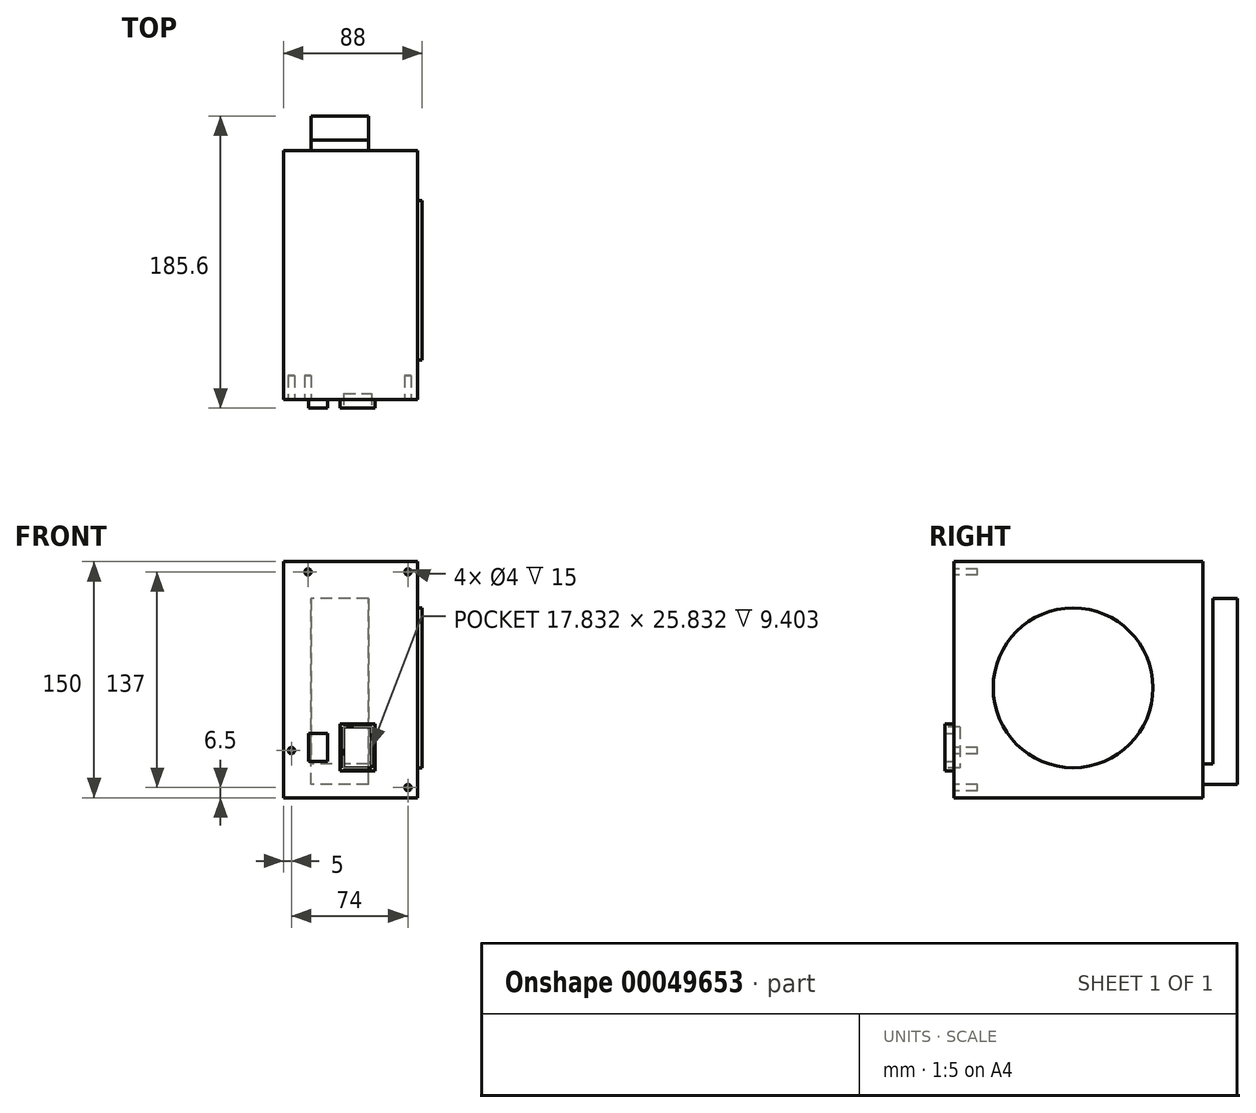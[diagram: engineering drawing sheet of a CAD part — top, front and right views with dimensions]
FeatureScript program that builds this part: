
annotation { "Feature Type Name" : "Feature", "Feature Type Description" : "" }
export const myFeature = defineFeature(function(context is Context, id is Id, definition is map)
    precondition{}
    {
        {
            var Q0;
            Q0=qCreatedBy(makeId("Front.planeOp"),FACE);
            var sketch = newSketch(context, id + "F0", { "sketchPlane" : qUnion([Q0])});
            skLineSegment(sketch, "E0.bottom", {"start": v(0, 0) * mm, "end": v(85, 0) * mm});
            skLineSegment(sketch, "E0.top", {"start": v(0, 150) * mm, "end": v(85, 150) * mm});
            skLineSegment(sketch, "E0.left", {"start": v(0, 0) * mm, "end": v(0, 150) * mm});
            skLineSegment(sketch, "E0.right", {"start": v(85, 0) * mm, "end": v(85, 150) * mm});
            skCircle(sketch, "E1", {"center": v(5, 30) * mm, "radius": 2 * mm});
            skCircle(sketch, "E2", {"center": v(15.5, 143.5) * mm, "radius": 2 * mm});
            skCircle(sketch, "E3", {"center": v(79, 143.5) * mm, "radius": 2 * mm});
            skCircle(sketch, "E4", {"center": v(79, 6.5) * mm, "radius": 2 * mm});
            skSolve(sketch);
        }
        {
            var Q0;
            Q0=makeQuery(id+"F0.imprint","IMPRINT",FACE,{"disambiguationData":[TD([[makeQuery(id+"F0.imprint","IMPRINT",EDGE,{"derivedFrom":sQuery(id+"F0.wireOp",EDGE,"E0.bottom")}),1.0]])]});
            var Q1;
            Q1=makeQuery(id+"F0.imprint","IMPRINT",FACE,{"disambiguationData":[TD([[makeQuery(id+"F0.imprint","IMPRINT",EDGE,{"derivedFrom":sQuery(id+"F0.wireOp",EDGE,"E2")}),1.0]])]});
            var Q2;
            Q2=makeQuery(id+"F0.imprint","IMPRINT",FACE,{"disambiguationData":[TD([[makeQuery(id+"F0.imprint","IMPRINT",EDGE,{"derivedFrom":sQuery(id+"F0.wireOp",EDGE,"E3")}),1.0]])]});
            var Q3;
            Q3=makeQuery(id+"F0.imprint","IMPRINT",FACE,{"disambiguationData":[TD([[makeQuery(id+"F0.imprint","IMPRINT",EDGE,{"derivedFrom":sQuery(id+"F0.wireOp",EDGE,"E4")}),1.0]])]});
            var Q4;
            Q4=makeQuery(id+"F0.imprint","IMPRINT",FACE,{"disambiguationData":[TD([[makeQuery(id+"F0.imprint","IMPRINT",EDGE,{"derivedFrom":sQuery(id+"F0.wireOp",EDGE,"E1")}),1.0]])]});
            extrude(context, id + "F1", {"entities" : qUnion([Q0, Q1, Q2, Q3, Q4]), "depth" : 158 * mm});
        }
        {
            var Q0;
            Q0=makeQuery(id+"F1.opExtrude","CAP_FACE",FACE,{"disambiguationData":[OSD([sQuery(id+"F0.wireOp",EDGE,"E0.bottom"),sQuery(id+"F0.wireOp",EDGE,"E0.top"),sQuery(id+"F0.wireOp",EDGE,"E0.left"),sQuery(id+"F0.wireOp",EDGE,"E0.right")])],"isStart":false});
            var sketch = newSketch(context, id + "F2", { "sketchPlane" : qUnion([Q0])});
            skCircle(sketch, "E5.0", {"center": v(79, 6.5) * mm, "radius": 2 * mm});
            skCircle(sketch, "E6.0", {"center": v(5, 30) * mm, "radius": 2 * mm});
            skCircle(sketch, "E7.0", {"center": v(15.5, 143.5) * mm, "radius": 2 * mm});
            skCircle(sketch, "E8.0", {"center": v(79, 143.5) * mm, "radius": 2 * mm});
            skSolve(sketch);
        }
        {
            var Q0;
            Q0 = qSketchRegion(id + "F2", true);
            extrude(context, id + "F3", {"entities" : qUnion([Q0]), "operationType" : NewBodyOperationType.REMOVE, "oppositeDirection" : true, "depth" : 15 * mm});
        }
        {
            var Q0;
            Q0=makeQuery(id+"F1.opExtrude","CAP_FACE",FACE,{"disambiguationData":[OSD([sQuery(id+"F0.wireOp",EDGE,"E0.bottom"),sQuery(id+"F0.wireOp",EDGE,"E0.top"),sQuery(id+"F0.wireOp",EDGE,"E0.left"),sQuery(id+"F0.wireOp",EDGE,"E0.right")])],"isStart":false});
            var sketch = newSketch(context, id + "F4", { "sketchPlane" : qUnion([Q0])});
            skLineSegment(sketch, "E9.bottom", {"start": v(58, 17) * mm, "end": v(36, 17) * mm});
            skLineSegment(sketch, "E9.top", {"start": v(58, 47) * mm, "end": v(36, 47) * mm});
            skLineSegment(sketch, "E9.left", {"start": v(58, 17) * mm, "end": v(58, 47) * mm});
            skLineSegment(sketch, "E9.right", {"start": v(36, 17) * mm, "end": v(36, 47) * mm});
            skLineSegment(sketch, "E10.bottom", {"start": v(28, 23) * mm, "end": v(16, 23) * mm});
            skLineSegment(sketch, "E10.top", {"start": v(28, 41) * mm, "end": v(16, 41) * mm});
            skLineSegment(sketch, "E10.left", {"start": v(28, 23) * mm, "end": v(28, 41) * mm});
            skLineSegment(sketch, "E10.right", {"start": v(16, 23) * mm, "end": v(16, 41) * mm});
            skSolve(sketch);
        }
        {
            var Q0;
            Q0=makeQuery(id+"F4.imprint","IMPRINT",FACE,{"disambiguationData":[TD([[makeQuery(id+"F4.imprint","IMPRINT",EDGE,{"derivedFrom":sQuery(id+"F4.wireOp",EDGE,"E10.bottom")}),-1.0]])]});
            var Q1;
            Q1=makeQuery(id+"F4.imprint","IMPRINT",FACE,{"disambiguationData":[TD([[makeQuery(id+"F4.imprint","IMPRINT",EDGE,{"derivedFrom":sQuery(id+"F4.wireOp",EDGE,"E9.bottom")}),-1.0]])]});
            extrude(context, id + "F5", {"entities" : qUnion([Q0, Q1]), "operationType" : NewBodyOperationType.ADD, "depth" : 5.6 * mm});
        }
        {
            var Q0;
            Q0=makeQuery(id+"F5.opExtrude","CAP_FACE",FACE,{"disambiguationData":[OSD([sQuery(id+"F4.wireOp",EDGE,"E9.bottom"),sQuery(id+"F4.wireOp",EDGE,"E9.top"),sQuery(id+"F4.wireOp",EDGE,"E9.left"),sQuery(id+"F4.wireOp",EDGE,"E9.right")])],"isStart":false});
            var sketch = newSketch(context, id + "F6", { "sketchPlane" : qUnion([Q0])});
            skLineSegment(sketch, "E11.0", {"start": v(38.08, 19.08) * mm, "end": v(55.92, 19.08) * mm});
            skLineSegment(sketch, "E11.1", {"start": v(38.08, 44.92) * mm, "end": v(38.08, 19.08) * mm});
            skLineSegment(sketch, "E11.2", {"start": v(55.92, 44.92) * mm, "end": v(38.08, 44.92) * mm});
            skLineSegment(sketch, "E11.3", {"start": v(55.92, 19.08) * mm, "end": v(55.92, 44.92) * mm});
            skSolve(sketch);
        }
        {
            var Q0;
            Q0=makeQuery(id+"F6.imprint","IMPRINT",FACE,{"disambiguationData":[TD([[makeQuery(id+"F6.imprint","IMPRINT",EDGE,{"derivedFrom":sQuery(id+"F6.wireOp",EDGE,"E11.0")}),1.0]])]});
            extrude(context, id + "F7", {"entities" : qUnion([Q0]), "operationType" : NewBodyOperationType.REMOVE, "oppositeDirection" : true, "depth" : 9.4 * mm});
        }
        {
            var Q0;
            Q0=makeQuery(id+"F1.opExtrude","SWEPT_FACE",FACE,{"disambiguationData":[OSD([sQuery(id+"F0.wireOp",EDGE,"E0.right")])]});
            var sketch = newSketch(context, id + "F8", { "sketchPlane" : qUnion([Q0])});
            skCircle(sketch, "E12", {"center": v(-82.33, 69.87) * mm, "radius": 50.72 * mm});
            skSolve(sketch);
        }
        {
            var Q0;
            Q0 = qSketchRegion(id + "F8", true);
            var Q1;
            Q1=makeQuery(id+"F8.imprint","IMPRINT",FACE,{"disambiguationData":[TD([[makeQuery(id+"F8.imprint","IMPRINT",EDGE,{"derivedFrom":sQuery(id+"F8.wireOp",EDGE,"E12")}),1.0]])]});
            extrude(context, id + "F9", {"entities" : qUnion([Q0, Q1]), "operationType" : NewBodyOperationType.ADD, "depth" : 3 * mm});
        }
        {
            var Q0;
            Q0=makeQuery(id+"F0.imprint","IMPRINT",FACE,{"disambiguationData":[TD([[makeQuery(id+"F0.imprint","IMPRINT",EDGE,{"derivedFrom":sQuery(id+"F0.wireOp",EDGE,"E0.bottom")}),1.0]])]});
            var sketch = newSketch(context, id + "F10", { "sketchPlane" : qUnion([Q0])});
            skLineSegment(sketch, "E13.bottom", {"start": v(53.93, 8.49) * mm, "end": v(17.55, 8.49) * mm});
            skLineSegment(sketch, "E13.top", {"start": v(53.93, 21.4) * mm, "end": v(17.55, 21.4) * mm});
            skLineSegment(sketch, "E13.left", {"start": v(53.93, 8.49) * mm, "end": v(53.93, 21.4) * mm});
            skLineSegment(sketch, "E13.right", {"start": v(17.55, 8.49) * mm, "end": v(17.55, 21.4) * mm});
            skSolve(sketch);
        }
        {
            var Q0;
            Q0 = qSketchRegion(id + "F10", true);
            extrude(context, id + "F11", {"entities" : qUnion([Q0]), "operationType" : NewBodyOperationType.ADD, "oppositeDirection" : true, "depth" : 22.01 * mm});
        }
        {
            var Q0;
            Q0=makeQuery(id+"F11.opExtrude","SWEPT_FACE",FACE,{"disambiguationData":[OSD([sQuery(id+"F10.wireOp",EDGE,"E13.top")])]});
            var sketch = newSketch(context, id + "F12", { "sketchPlane" : qUnion([Q0])});
            skLineSegment(sketch, "E14.bottom", {"start": v(53.93, 22.01) * mm, "end": v(17.55, 22.01) * mm});
            skLineSegment(sketch, "E14.top", {"start": v(53.93, 6.55) * mm, "end": v(17.55, 6.55) * mm});
            skLineSegment(sketch, "E14.left", {"start": v(53.93, 22.01) * mm, "end": v(53.93, 6.55) * mm});
            skLineSegment(sketch, "E14.right", {"start": v(17.55, 22.01) * mm, "end": v(17.55, 6.55) * mm});
            skSolve(sketch);
        }
        {
            var Q0;
            Q0=makeQuery(id+"F12.imprint","IMPRINT",FACE,{"disambiguationData":[TD([[makeQuery(id+"F12.imprint","IMPRINT",EDGE,{"derivedFrom":sQuery(id+"F12.wireOp",EDGE,"E14.bottom")}),1.0]])]});
            extrude(context, id + "F13", {"entities" : qUnion([Q0]), "operationType" : NewBodyOperationType.ADD, "depth" : 105.27 * mm});
        }
    });
